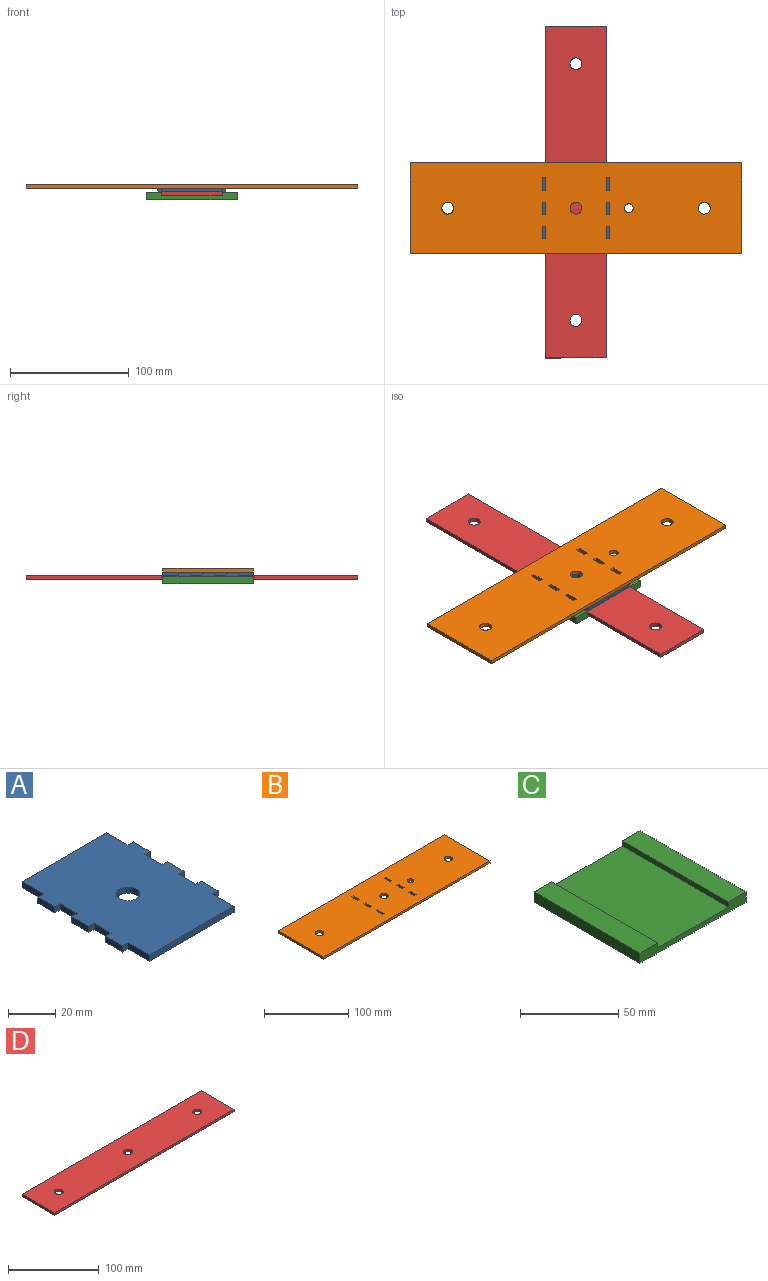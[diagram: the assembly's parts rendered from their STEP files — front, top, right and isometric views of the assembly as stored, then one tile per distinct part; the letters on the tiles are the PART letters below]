
ASSEMBLY  parts=4 mates=3
PART A: 31 faces, bbox 57.2x76.2x3.2 mm
  f0: plane 3.18x3.18mm, normal (0,1,0), area 10.1mm2, adj f1,f27,f29,f30
  f1: plane 10.16x3.18mm, normal (-1,0,0), area 32.3mm2, adj f0,f2,f29,f30
  f2: plane 3.18x3.18mm, normal (0,-1,0), area 10.1mm2, adj f1,f3,f29,f30
  f3: plane 10.16x3.18mm, normal (-1,0,0), area 32.3mm2, adj f2,f4,f29,f30
  f4: plane 3.18x3.18mm, normal (0,1,0), area 10.1mm2, adj f3,f5,f29,f30
  f5: plane 10.16x3.18mm, normal (-1,0,0), area 32.3mm2, adj f4,f6,f29,f30
  f6: plane 3.18x3.18mm, normal (0,-1,0), area 10.1mm2, adj f5,f7,f29,f30
  f7: plane 10.16x3.18mm, normal (-1,0,0), area 32.3mm2, adj f6,f8,f29,f30
  f8: plane 3.18x3.18mm, normal (0,1,0), area 10.1mm2, adj f7,f9,f29,f30
  f9: plane 10.16x3.18mm, normal (-1,0,0), area 32.3mm2, adj f8,f10,f29,f30
  f10: plane 3.18x3.18mm, normal (0,-1,0), area 10.1mm2, adj f9,f11,f29,f30
  f11: plane 12.7x3.18mm, normal (-1,0,0), area 40.3mm2, adj f10,f12,f29,f30
  f12: plane 50.8x3.18mm, normal (0,-1,0), area 161.3mm2, adj f11,f13,f29,f30
  f13: plane 12.7x3.18mm, normal (1,0,0), area 40.3mm2, adj f12,f14,f29,f30
  f14: plane 3.18x3.18mm, normal (0,-1,0), area 10.1mm2, adj f13,f15,f29,f30
  f15: plane 10.16x3.18mm, normal (1,0,0), area 32.3mm2, adj f14,f16,f29,f30
  f16: plane 3.18x3.18mm, normal (0,1,0), area 10.1mm2, adj f15,f17,f29,f30
  f17: plane 10.16x3.18mm, normal (1,0,0), area 32.3mm2, adj f16,f18,f29,f30
  f18: plane 3.18x3.18mm, normal (0,-1,0), area 10.1mm2, adj f17,f19,f29,f30
  f19: plane 10.16x3.18mm, normal (1,0,0), area 32.3mm2, adj f18,f20,f29,f30
  f20: plane 3.18x3.18mm, normal (0,1,0), area 10.1mm2, adj f19,f21,f29,f30
  f21: plane 10.16x3.18mm, normal (1,0,0), area 32.3mm2, adj f20,f22,f29,f30
  f22: plane 3.18x3.18mm, normal (0,-1,0), area 10.1mm2, adj f21,f23,f29,f30
  f23: plane 10.16x3.18mm, normal (1,0,0), area 32.3mm2, adj f22,f24,f29,f30
  f24: plane 3.18x3.18mm, normal (0,1,0), area 10.1mm2, adj f23,f25,f29,f30
  f25: plane 12.7x3.18mm, normal (1,0,0), area 40.3mm2, adj f24,f26,f29,f30
  f26: plane 50.8x3.18mm, normal (0,1,0), area 161.3mm2, adj f25,f27,f29,f30
  f27: plane 12.7x3.18mm, normal (-1,0,0), area 40.3mm2, adj f0,f26,f29,f30
  f28: cylinder r=4.99mm len=9.98mm, axis (0,0,-1), area 99.6mm2, adj f29,f30
  f29: plane 76.2x57.15mm, normal (0,0,1), area 3986.2mm2, adj f0,f1,f2,f3,f4,f5,f6,f7
  f30: plane 76.2x57.15mm, normal (0,0,-1), area 3986.2mm2, adj f0,f1,f2,f3,f4,f5,f6,f7
PART B: 34 faces, bbox 279.4x76.2x3.2 mm
  f0: plane 279.4x3.18mm, normal (0,1,0), area 887.1mm2, adj f1,f31,f32,f33
  f1: plane 76.2x3.18mm, normal (-1,0,0), area 241.9mm2, adj f0,f2,f32,f33
  f2: plane 279.4x3.18mm, normal (0,-1,0), area 887.1mm2, adj f1,f31,f32,f33
  f3: plane 10.16x3.18mm, normal (1,0,0), area 32.3mm2, adj f4,f21,f32,f33
  f4: plane 3.18x3.18mm, normal (0,-1,0), area 10.1mm2, adj f3,f5,f32,f33
  f5: plane 10.16x3.18mm, normal (-1,0,0), area 32.3mm2, adj f4,f21,f32,f33
  f6: plane 10.16x3.18mm, normal (1,0,0), area 32.3mm2, adj f7,f22,f32,f33
  f7: plane 3.18x3.18mm, normal (0,-1,0), area 10.1mm2, adj f6,f8,f32,f33
  f8: plane 10.16x3.18mm, normal (-1,0,0), area 32.3mm2, adj f7,f22,f32,f33
  f9: plane 10.16x3.18mm, normal (1,0,0), area 32.3mm2, adj f10,f23,f32,f33
  f10: plane 3.18x3.18mm, normal (0,-1,0), area 10.1mm2, adj f9,f11,f32,f33
  f11: plane 10.16x3.18mm, normal (-1,0,0), area 32.3mm2, adj f10,f23,f32,f33
  f12: plane 10.16x3.18mm, normal (1,0,0), area 32.3mm2, adj f13,f24,f32,f33
  f13: plane 3.18x3.18mm, normal (0,-1,0), area 10.1mm2, adj f12,f14,f32,f33
  f14: plane 10.16x3.18mm, normal (-1,0,0), area 32.3mm2, adj f13,f24,f32,f33
  f15: plane 10.16x3.18mm, normal (1,0,0), area 32.3mm2, adj f16,f25,f32,f33
  f16: plane 3.18x3.18mm, normal (0,-1,0), area 10.1mm2, adj f15,f17,f32,f33
  f17: plane 10.16x3.18mm, normal (-1,0,0), area 32.3mm2, adj f16,f25,f32,f33
  f18: plane 3.18x3.18mm, normal (0,-1,0), area 10.1mm2, adj f19,f30,f32,f33
  f19: plane 10.16x3.18mm, normal (-1,0,0), area 32.3mm2, adj f18,f20,f32,f33
  f20: plane 3.18x3.18mm, normal (0,1,0), area 10.1mm2, adj f19,f30,f32,f33
  f21: plane 3.18x3.18mm, normal (0,1,0), area 10.1mm2, adj f3,f5,f32,f33
  f22: plane 3.18x3.18mm, normal (0,1,0), area 10.1mm2, adj f6,f8,f32,f33
  f23: plane 3.18x3.18mm, normal (0,1,0), area 10.1mm2, adj f9,f11,f32,f33
  f24: plane 3.18x3.18mm, normal (0,1,0), area 10.1mm2, adj f12,f14,f32,f33
  f25: plane 3.18x3.18mm, normal (0,1,0), area 10.1mm2, adj f15,f17,f32,f33
  f26: cylinder r=3.75mm len=7.49mm, axis (0,0,-1), area 74.7mm2, adj f32,f33
  f27: cylinder r=4.99mm len=9.98mm, axis (0,0,-1), area 99.6mm2, adj f32,f33
  f28: cylinder r=4.99mm len=9.98mm, axis (0,0,-1), area 99.6mm2, adj f32,f33
  f29: cylinder r=4.99mm len=9.98mm, axis (0,0,-1), area 99.6mm2, adj f32,f33
  f30: plane 10.16x3.18mm, normal (1,0,0), area 32.3mm2, adj f18,f20,f32,f33
  f31: plane 76.2x3.18mm, normal (1,0,0), area 241.9mm2, adj f0,f2,f32,f33
  f32: plane 279.4x76.2mm, normal (0,0,1), area 20817.9mm2, adj f0,f1,f2,f3,f4,f5,f6,f7
  f33: plane 279.4x76.2mm, normal (0,0,-1), area 20817.9mm2, adj f0,f1,f2,f3,f4,f5,f6,f7
PART C: 10 faces, bbox 76.2x76.2x6.4 mm
  f0: plane 76.2x50.8mm, normal (0,0,1), area 3871mm2, adj f1,f3,f6,f8
  f1: plane 76.2x6.35mm, normal (0,1,0), area 322.6mm2, adj f0,f2,f4,f5,f6,f7,f8,f9
  f2: plane 76.2x6.35mm, normal (-1,0,0), area 483.9mm2, adj f1,f3,f5,f7
  f3: plane 76.2x6.35mm, normal (0,-1,0), area 322.6mm2, adj f0,f2,f4,f5,f6,f7,f8,f9
  f4: plane 76.2x6.35mm, normal (1,0,0), area 483.9mm2, adj f1,f3,f5,f9
  f5: plane 76.2x76.2mm, normal (0,0,-1), area 5806.4mm2, adj f1,f2,f3,f4
  f6: plane 76.2x3.18mm, normal (1,0,0), area 241.9mm2, adj f0,f1,f3,f7
  f7: plane 76.2x12.7mm, normal (0,0,1), area 967.7mm2, adj f1,f2,f3,f6
  f8: plane 76.2x3.18mm, normal (-1,0,0), area 241.9mm2, adj f0,f1,f3,f9
  f9: plane 76.2x12.7mm, normal (0,0,1), area 967.7mm2, adj f1,f3,f4,f8
PART D: 9 faces, bbox 279.4x50.8x3.2 mm
  f0: plane 279.4x3.18mm, normal (0,1,0), area 887.1mm2, adj f1,f6,f7,f8
  f1: plane 50.8x3.18mm, normal (-1,0,0), area 161.3mm2, adj f0,f2,f7,f8
  f2: plane 279.4x3.18mm, normal (0,-1,0), area 887.1mm2, adj f1,f6,f7,f8
  f3: cylinder r=4.99mm len=9.98mm, axis (0,0,-1), area 99.6mm2, adj f7,f8
  f4: cylinder r=4.99mm len=9.98mm, axis (0,0,-1), area 99.6mm2, adj f7,f8
  f5: cylinder r=4.99mm len=9.98mm, axis (0,0,-1), area 99.6mm2, adj f7,f8
  f6: plane 50.8x3.18mm, normal (1,0,0), area 161.3mm2, adj f0,f2,f7,f8
  f7: plane 279.4x50.8mm, normal (0,0,1), area 13958.7mm2, adj f0,f1,f2,f3,f4,f5,f6
  f8: plane 279.4x50.8mm, normal (0,0,-1), area 13958.7mm2, adj f0,f1,f2,f3,f4,f5,f6
PLACE A t=(-4.65,-1.65,46.12)mm
PLACE B t=(-4.56,-1.65,49.29)mm
PLACE C t=(-4.65,-1.65,39.77)mm fixed
PLACE D rot(axis=(0,0,-1),90deg) t=(-4.65,11.98,42.94)mm
MATE fastened A.f28 <-> B.f33  axis (0,0,1) through (-4.65,-1.65,49.29)mm
MATE planar D.f4 <-> C.f0  axis (0,0,-1) through (-4.65,11.98,42.94)mm
MATE planar D.f2 <-> C.f6  axis (-1,0,0) through (-30.05,11.98,44.53)mm
